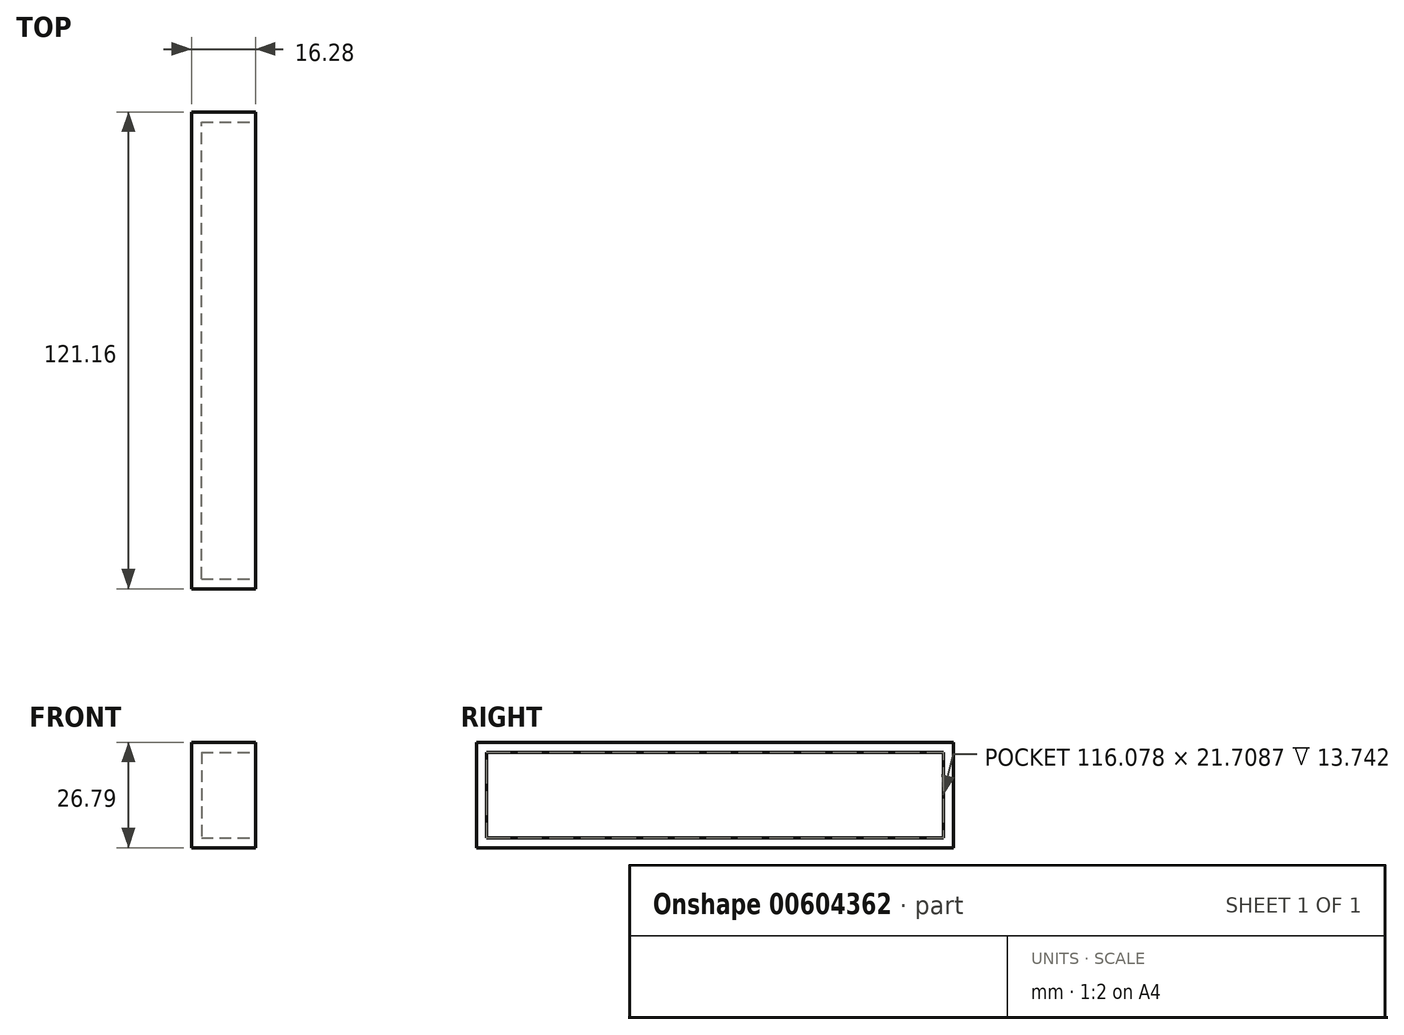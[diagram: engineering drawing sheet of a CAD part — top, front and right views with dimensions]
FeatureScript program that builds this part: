
annotation { "Feature Type Name" : "Feature", "Feature Type Description" : "" }
export const myFeature = defineFeature(function(context is Context, id is Id, definition is map)
    precondition{}
    {
        {
            var Q0;
            Q0=qCreatedBy(makeId("Front.planeOp"),FACE);
            var sketch = newSketch(context, id + "F0", { "sketchPlane" : qUnion([Q0])});
            skLineSegment(sketch, "E0.bottom", {"start": v(-62.88, 42.37) * mm, "end": v(-46.6, 42.37) * mm});
            skLineSegment(sketch, "E0.top", {"start": v(-62.88, 26.5) * mm, "end": v(-46.6, 26.5) * mm});
            skLineSegment(sketch, "E0.left", {"start": v(-62.88, 42.37) * mm, "end": v(-62.88, 26.5) * mm});
            skLineSegment(sketch, "E0.right", {"start": v(-46.6, 42.37) * mm, "end": v(-46.6, 26.5) * mm});
            skLineSegment(sketch, "E1.bottom", {"start": v(-11.9, -23.46) * mm, "end": v(-2.9, -23.46) * mm});
            skLineSegment(sketch, "E1.top", {"start": v(-11.9, -26.86) * mm, "end": v(-2.9, -26.86) * mm});
            skLineSegment(sketch, "E1.left", {"start": v(-11.9, -23.46) * mm, "end": v(-11.9, -26.86) * mm});
            skLineSegment(sketch, "E1.right", {"start": v(-2.9, -23.46) * mm, "end": v(-2.9, -26.86) * mm});
            skSolve(sketch);
        }
        {
            var Q0;
            Q0=makeQuery(id+"F0.imprint","IMPRINT",FACE,{"disambiguationData":[TD([[makeQuery(id+"F0.imprint","IMPRINT",EDGE,{"derivedFrom":sQuery(id+"F0.wireOp",EDGE,"E0.bottom")}),-1.0]])]});
            extrude(context, id + "F1", {"entities" : qUnion([Q0]), "depth" : 121.16 * mm, "offsetDistance" : 25.4 * mm});
        }
        {
            var Q0;
            Q0=makeQuery(id+"F1.opExtrude","SWEPT_FACE",FACE,{"disambiguationData":[OSD([sQuery(id+"F0.wireOp",EDGE,"E0.right")])]});
            var Q1;
            Q1=makeQuery(id+"F1.opExtrude","SWEPT_FACE",FACE,{"disambiguationData":[OSD([sQuery(id+"F0.wireOp",EDGE,"E0.bottom")])]});
            loft(context, id + "F2", {"sheetProfilesArray" : [{ "sheetProfileEntities" : qUnion([Q0]) }, { "sheetProfileEntities" : qUnion([Q1]) }]});
        }
        {
            var Q0;
            Q0=makeQuery(id+"F1.opExtrude","SWEPT_FACE",FACE,{"disambiguationData":[OSD([sQuery(id+"F0.wireOp",EDGE,"E0.bottom")])]});
            extrude(context, id + "F3", {"entities" : qUnion([Q0]), "operationType" : NewBodyOperationType.ADD, "depth" : 10.92 * mm, "offsetDistance" : 25.4 * mm});
        }
        {
            var Q0;
            {var subQ0=sQuery(id+"F0.wireOp",EDGE,"E0.right");Q0=makeQuery(id+"F3.boolean.opBoolean","MERGE",FACE,{"derivedFrom":[makeQuery(id+"F1.opExtrude","SWEPT_FACE",FACE,{"disambiguationData":[OSD([subQ0])]}),makeQuery(id+"F3.opExtrude","SWEPT_FACE",FACE,{"disambiguationData":[OSD([sQuery(id+"F0.wireOp",EDGE,"E0.bottom"),subQ0])]})]});}
            shell(context, id + "F4", {"entities" : qUnion([Q0]), "thickness" : 2.54 * mm});
        }
    });
